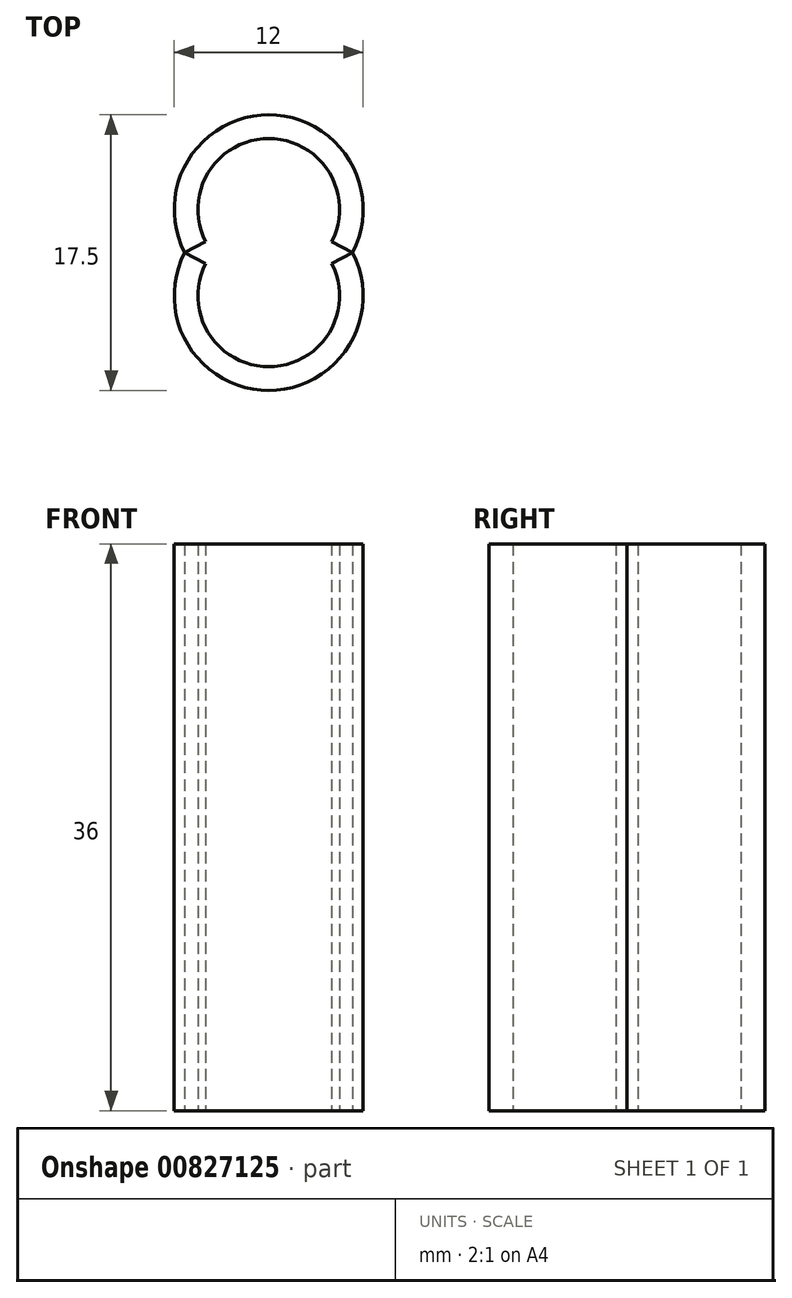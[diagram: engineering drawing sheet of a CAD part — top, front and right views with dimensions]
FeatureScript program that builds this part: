
annotation { "Feature Type Name" : "Feature", "Feature Type Description" : "" }
export const myFeature = defineFeature(function(context is Context, id is Id, definition is map)
    precondition{}
    {
        {
            var Q0;
            Q0=qCreatedBy(makeId("Top.planeOp"),FACE);
            var sketch = newSketch(context, id + "F0", { "sketchPlane" : qUnion([Q0])});
            skArc(sketch, "E0", {"start": v(4, -2.06) * mm, "mid": v(0, 4.5) * mm, "end": v(-4, -2.06) * mm});
            skLineSegment(sketch, "E1", {"start": v(-4, -2.06) * mm, "end": v(4, -2.06) * mm, "construction": true});
            skArc(sketch, "E2", {"start": v(5.33, -2.75) * mm, "mid": v(0, 6) * mm, "end": v(-5.33, -2.75) * mm});
            skLineSegment(sketch, "E3", {"start": v(4, -2.06) * mm, "end": v(5.33, -2.75) * mm});
            skLineSegment(sketch, "E4", {"start": v(-4, -2.06) * mm, "end": v(-5.33, -2.75) * mm});
            skSolve(sketch);
        }
        {
            var Q0;
            Q0=makeQuery(id+"F0.imprint","IMPRINT",FACE,{"disambiguationData":[TD([[makeQuery(id+"F0.imprint","IMPRINT",EDGE,{"derivedFrom":sQuery(id+"F0.wireOp",EDGE,"E0")}),-1.0]])]});
            extrude(context, id + "F1", {"entities" : qUnion([Q0]), "depth" : 36 * mm, "offsetDistance" : 25 * mm});
        }
        {
            var Q0;
            Q0=qCreatedBy(makeId("Front.planeOp"),FACE);
            var Q1;
            Q1=makeQuery(id+"F1.opExtrude","CAP_VERTEX",VERTEX,{"disambiguationData":[OSD([sQuery(id+"F0.wireOp",EDGE,"E2"),sQuery(id+"F0.wireOp",EDGE,"E4")])],"isStart":false});
            cPlane(context, id + "F2", {"entities" : qUnion([Q0, Q1]), "cplaneType" : CPlaneType.PLANE_POINT, "offset" : 25 * mm, "width" : 150 * mm, "height" : 150 * mm});
        }
        {
            var Q0;
            Q0=makeQuery(id+"F1.opExtrude","SWEPT_BODY",BODY,{"disambiguationData":[OSD([sQuery(id+"F0.wireOp",EDGE,"E0"),sQuery(id+"F0.wireOp",EDGE,"E2"),sQuery(id+"F0.wireOp",EDGE,"E3"),sQuery(id+"F0.wireOp",EDGE,"E4")])]});
            var Q1;
            Q1=qCreatedBy(id+"F2.planeOp",FACE);
            mirror(context, id + "F3", {"entities" : qUnion([Q0]), "mirrorPlane" : qUnion([Q1])});
        }
    });
